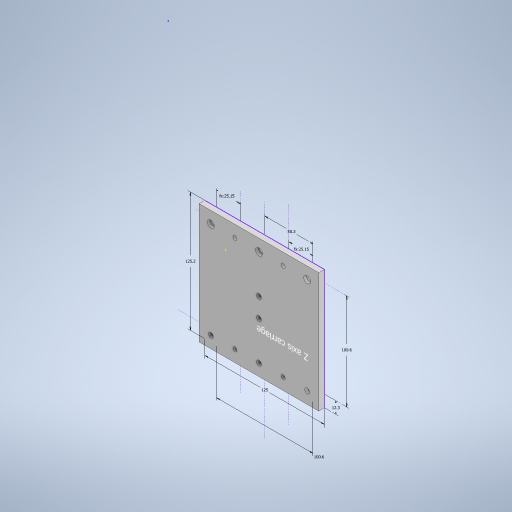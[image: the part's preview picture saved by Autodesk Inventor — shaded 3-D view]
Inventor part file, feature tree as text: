
AUTODESK INVENTOR PART (.ipt)
format: ipt  version: 2023.2 (Build 272271000, 271)  size: 635,392 bytes
history: native  units: mm
features: sketch x4, hole x4, other x3, extrude x1, reference x1
ambient origin geometry x8: Origin, YZ Plane, XZ Plane, XY Plane, X Axis, Y Axis, Z Axis, Center Point
bodies: Solid1 (feature_tree)
feature tree (13):
  sketch  "Sketch1"  dims[d0=125.0mm d1=125.2mm d6=100.6mm d11=6.0mm d12=0.0mm d48=12.3mm]
  extrude  "Extrusion1"  Depth=6.0mm
  hole  "Hole6"  [1 undecoded]
  sketch  "Sketch2"  dims[d49=100.6mm d50=50.3mm]
  sketch  "Sketch3"  dims[d51=5.1mm d52=6.0mm d53=9.2mm d54=3.0mm d55=90.0deg d56=8.0mm d57=20.594885mm]
  hole  "Hole7"  [1 undecoded]
  hole  "Hole8"  [1 undecoded]
  hole  "Hole9"  [1 undecoded]
  reference  "Reference7"
  sketch  "Sketch5"  dims[d58=7.2mm d59=6.0mm d60=12.25mm d61=3.0mm d62=90.0deg d63=8.0mm d64=20.594885mm d65=5.1mm d66=6.0mm d67=9.2mm d68=3.0mm d69=90.0deg d70=8.0mm d71=20.594885mm d72=25.15mm d73=25.15mm d74=4.2mm d75=6.0mm d76=9.2mm d77=2.0mm d78=90.0deg d79=8.0mm d80=20.594885mm d81=10.0mm d82=10.0mm]
  parser-record x1  (decoder bookkeeping rows leaked as tree rows — omitted from the tree; the rows remain in map.json)
  other  "Main Assembly.iam"
  other  "Z axis carriage small 2:1"
note: 4 required parameter values undecoded (feature->parameter linkage not recoverable at this tier; creation-order binding heuristic only, values carry confidence <= 0.55)
note: 1 file-system path scrubbed to <path> (originals preserved in map.json)
